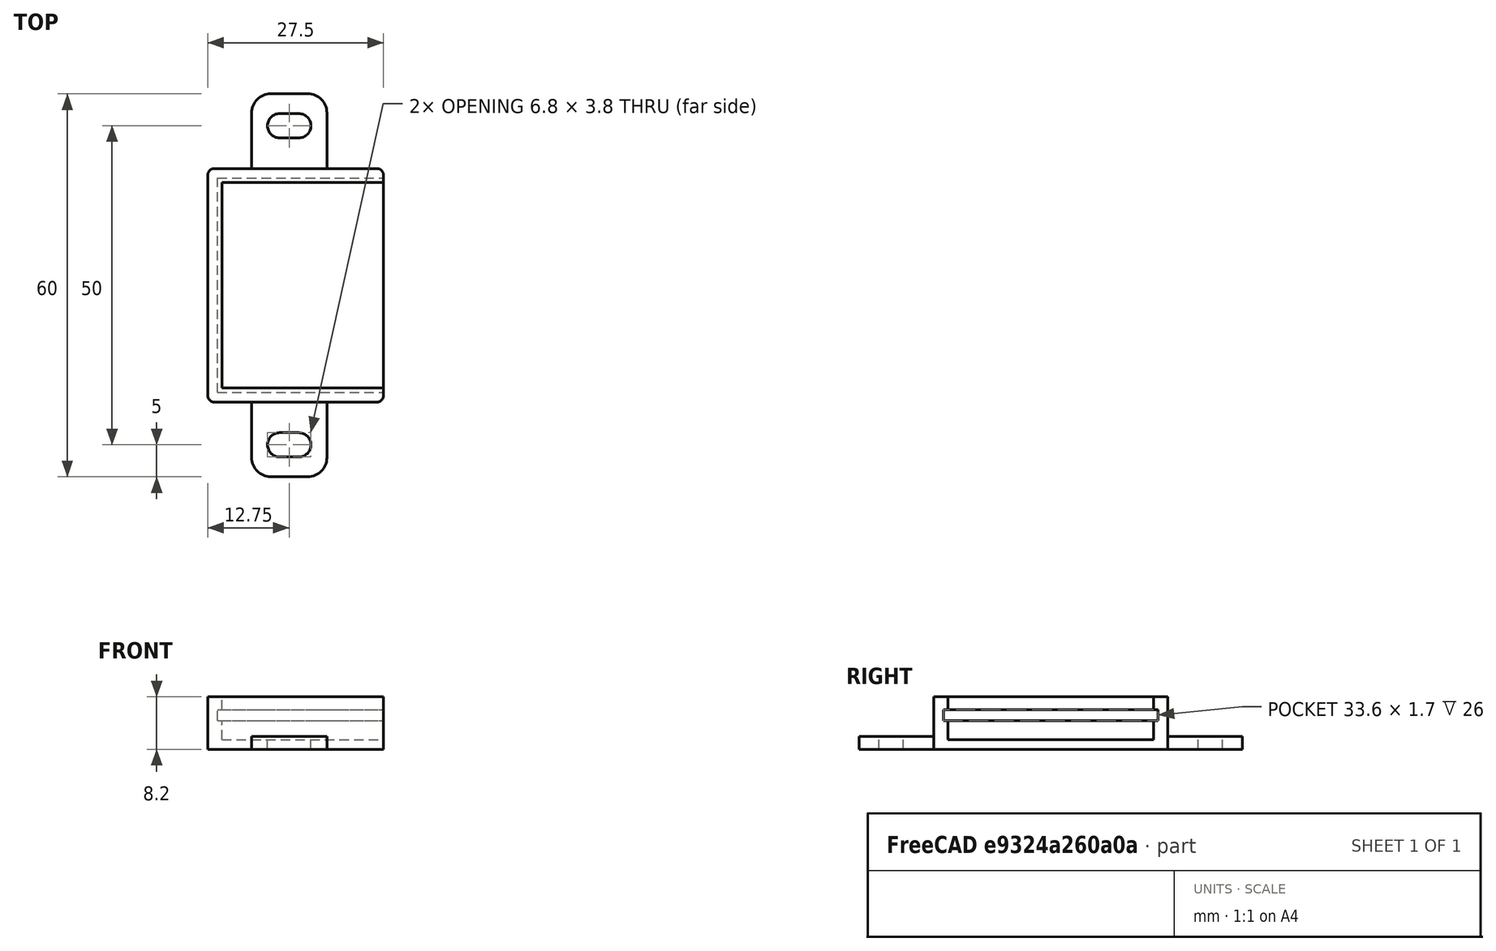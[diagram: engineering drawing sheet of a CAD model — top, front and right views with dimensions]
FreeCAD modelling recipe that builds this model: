
FCSTD DOCUMENT  (FreeCAD 0.19R23578 (Git))
Label: charger_hw
License: FreeArt
LicenseURL: http://artlibre.org/licence/lal
objects: Part::Box×3, Part::MultiFuse×2, Spreadsheet::Sheet×1, Part::Fillet×1, Part::Feature×1, Part::Cut×1, App::Part×1
note: 8 computed .brp shape members not serialized (recipe doc carries the construction recipe); baked Part::Feature solids carry a one-line shape summary decoded from their .brp

FEATURE [Spreadsheet::Sheet] Spreadsheet  label="p"
  cells = A1=pcb_x; B1(pcb_x)=26; A2=pcb_y; B2(pcb_y)=33.6; A3=pcb_z; B3(pcb_z)=1.7; A4=pcb_under; B4(pcb_under)=3; A5=side_wall; B5(side_wall)=1.5; A6=pcb_side_lane; B6(pcb_side_lane)=0.7; A7=bottom_wall; B7(bottom_wall)=1.5; A8=pcb_above; B8(pcb_above)=2
FEATURE [Part::Box] Box  label="external cube"
  AttacherType = Attacher::AttachEngine3D
  Height = 8.2
  Length = 27.5
  Width = 36.6
  expr: Length = <<p>>.pcb_x + <<p>>.side_wall
  expr: Width = <<p>>.pcb_y + 2 * <<p>>.side_wall
  expr: Height = <<p>>.bottom_wall + <<p>>.pcb_under + <<p>>.pcb_z + <<p>>.pcb_above
FEATURE [Part::Box] Box006  label="internal cube"
  AttacherType = Attacher::AttachEngine3D
  Height = 6.7
  Length = 26.1
  Placement = pos=(2.2,2.2,1.5) rot=(0,0,1;0rad)
  Width = 32.2
  expr: Length = <<p>>.pcb_x - 2 * <<p>>.pcb_side_lane + <<p>>.side_wall
  expr: Width = <<p>>.pcb_y - 2 * <<p>>.pcb_side_lane
  expr: Height = <<p>>.pcb_under + <<p>>.pcb_z + <<p>>.pcb_above
  expr: .Placement.Base.z = <<p>>.bottom_wall
  expr: .Placement.Base.x = <<p>>.side_wall + <<p>>.pcb_side_lane
  expr: .Placement.Base.y = <<p>>.side_wall + <<p>>.pcb_side_lane
FEATURE [Part::Box] Box007  label="pcb extract cube"
  AttacherType = Attacher::AttachEngine3D
  Height = 1.7
  Length = 26
  Placement = pos=(1.5,1.5,4.5) rot=(0,0,1;0rad)
  Width = 33.6
  expr: Height = <<p>>.pcb_z
  expr: .Placement.Base.z = <<p>>.bottom_wall + <<p>>.pcb_under
  expr: Width = <<p>>.pcb_y
  expr: Length = <<p>>.pcb_x
  expr: .Placement.Base.x = <<p>>.side_wall
  expr: .Placement.Base.y = <<p>>.side_wall
FEATURE [Part::MultiFuse] Fusion  label="extract fusion"
  Shapes = -> [Box006,Box007]
FEATURE [Part::Fillet] Fillet  label="external fillet"
  Base = -> Box
  Edges = 4 edges r=1: [Edge1,Edge3,Edge5,Edge7]
FEATURE [Part::Feature] Cut002001  label="attach plane y dir001"
  Placement = pos=(6.85,-11.7,0) rot=(0,0,1;0rad)
  shape: bbox 11.8 x 60 x 2 mm, 20 faces (baked)
FEATURE [Part::MultiFuse] Fusion001  label="solid fusion"
  Shapes = -> [Fillet,Cut002001]
FEATURE [Part::Cut] Cut  label="body cut"
  Base = -> Fusion001
  Tool = -> Fusion
FEATURE [App::Part] Part  label="charger hw pcb box part"
  Group = -> [Box,Fillet,Fusion001,Fusion,Box007,Box006,Cut]
  Origin = -> Origin
